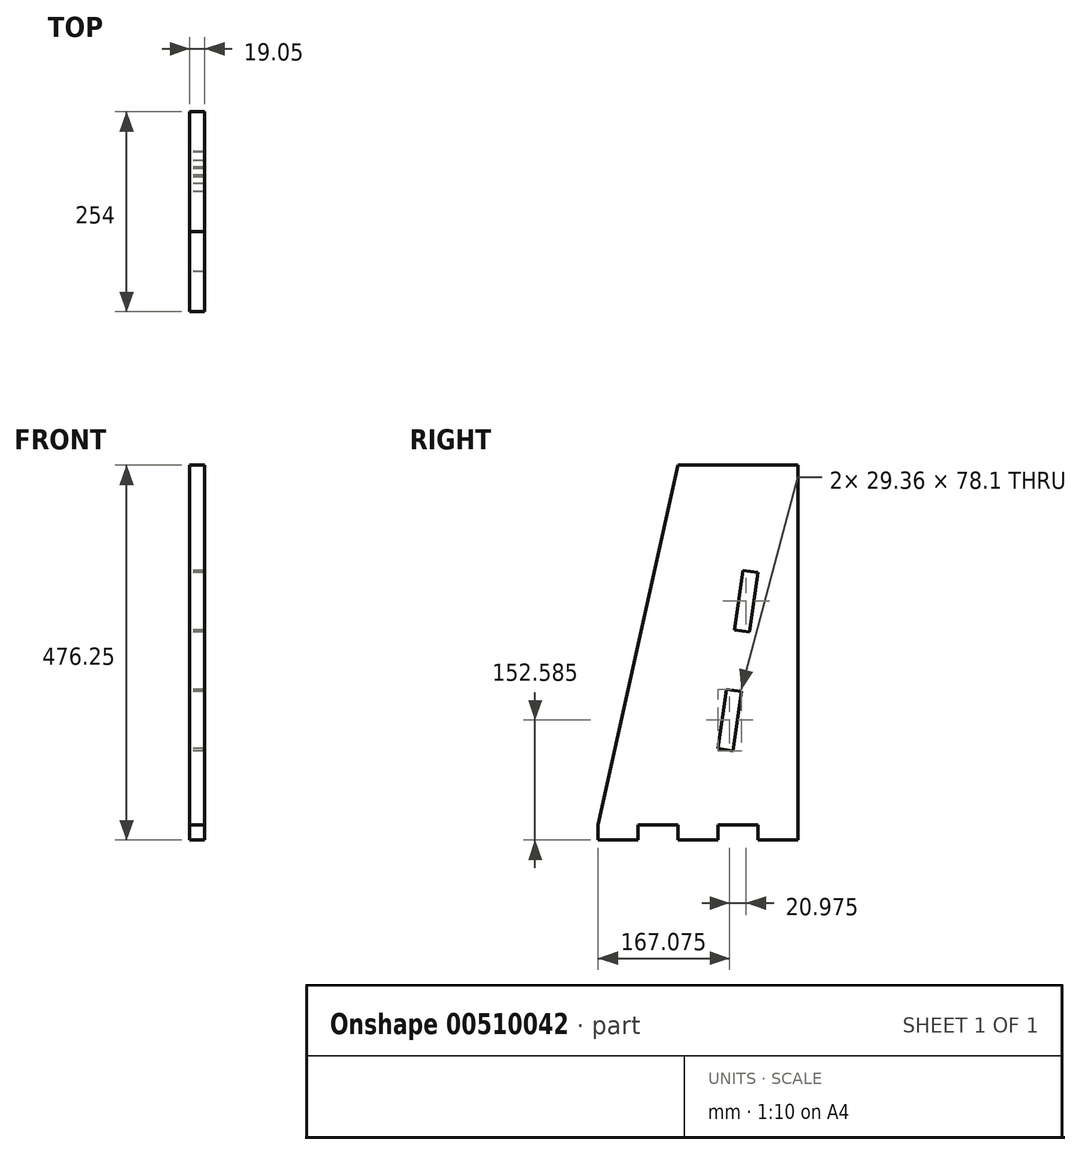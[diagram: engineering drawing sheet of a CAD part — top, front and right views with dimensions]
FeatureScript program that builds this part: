
annotation { "Feature Type Name" : "Feature", "Feature Type Description" : "" }
export const myFeature = defineFeature(function(context is Context, id is Id, definition is map)
    precondition{}
    {
        {
            var Q0;
            Q0=qCreatedBy(makeId("Right.planeOp"),FACE);
            var sketch = newSketch(context, id + "F0", { "sketchPlane" : qUnion([Q0])});
            skLineSegment(sketch, "E0", {"start": v(-38.45, 45.53) * mm, "end": v(113.95, 45.53) * mm});
            skLineSegment(sketch, "E1", {"start": v(113.95, 45.53) * mm, "end": v(113.95, -411.67) * mm});
            skLineSegment(sketch, "E2", {"start": v(-38.45, 45.53) * mm, "end": v(-140.05, -411.67) * mm});
            skLineSegment(sketch, "E3.top", {"start": v(113.95, -430.72) * mm, "end": v(63.15, -430.72) * mm});
            skLineSegment(sketch, "E3.left", {"start": v(113.95, -411.67) * mm, "end": v(113.95, -430.72) * mm});
            skLineSegment(sketch, "E3.right", {"start": v(63.15, -411.67) * mm, "end": v(63.15, -430.72) * mm});
            skLineSegment(sketch, "E4.1.0.0", {"start": v(12.35, -411.67) * mm, "end": v(12.35, -430.72) * mm});
            skLineSegment(sketch, "E4.1.0.1", {"start": v(-38.45, -411.67) * mm, "end": v(-38.45, -430.72) * mm});
            skLineSegment(sketch, "E4.1.0.2", {"start": v(12.35, -430.72) * mm, "end": v(-38.45, -430.72) * mm});
            skLineSegment(sketch, "E4.2.0.0", {"start": v(-89.25, -411.67) * mm, "end": v(-89.25, -430.72) * mm});
            skLineSegment(sketch, "E4.2.0.1", {"start": v(-140.05, -411.67) * mm, "end": v(-140.05, -430.72) * mm});
            skLineSegment(sketch, "E4.2.0.2", {"start": v(-89.25, -430.72) * mm, "end": v(-140.05, -430.72) * mm});
            skLineSegment(sketch, "E4.direction1", {"start": v(63.15, -430.72) * mm, "end": v(-38.45, -430.72) * mm, "construction": true});
            skLineSegment(sketch, "E5", {"start": v(-89.25, -411.67) * mm, "end": v(-38.45, -411.67) * mm});
            skLineSegment(sketch, "E6", {"start": v(12.35, -411.67) * mm, "end": v(63.15, -411.67) * mm});
            skLineSegment(sketch, "E7.bottom", {"start": v(113.95, 45.53) * mm, "end": v(133, 45.53) * mm});
            skLineSegment(sketch, "E7.left", {"start": v(113.95, 45.53) * mm, "end": v(113.95, -30.67) * mm});
            skLineSegment(sketch, "E8.right", {"start": v(113.95, -30.67) * mm, "end": v(113.95, -106.87) * mm});
            skLineSegment(sketch, "E9.bottom", {"start": v(62.68, -90.76) * mm, "end": v(43.8, -88.14) * mm});
            skLineSegment(sketch, "E9.top", {"start": v(52.2, -166.23) * mm, "end": v(33.32, -163.61) * mm});
            skLineSegment(sketch, "E9.right", {"start": v(43.8, -88.14) * mm, "end": v(33.32, -163.61) * mm});
            skLineSegment(sketch, "E10.top", {"start": v(41.7, -241.7) * mm, "end": v(22.83, -239.09) * mm});
            skLineSegment(sketch, "E10.right", {"start": v(113.95, -183.07) * mm, "end": v(113.95, -259.27) * mm});
            skLineSegment(sketch, "E11.top", {"start": v(31.22, -317.18) * mm, "end": v(12.35, -314.56) * mm});
            skLineSegment(sketch, "E11.right", {"start": v(22.83, -239.09) * mm, "end": v(12.35, -314.56) * mm});
            skLineSegment(sketch, "E12.right", {"start": v(113.95, -335.47) * mm, "end": v(113.95, -411.67) * mm});
            skLineSegment(sketch, "E13.left", {"start": v(41.7, -241.7) * mm, "end": v(31.22, -317.18) * mm});
            skLineSegment(sketch, "E14.left", {"start": v(62.68, -90.76) * mm, "end": v(52.2, -166.23) * mm});
            skSolve(sketch);
        }
        {
            var Q0;
            Q0=makeQuery(id+"F0.imprint","IMPRINT",FACE,{"disambiguationData":[TD([[makeQuery(id+"F0.imprint","IMPRINT",EDGE,{"derivedFrom":sQuery(id+"F0.wireOp",EDGE,"E0")}),-1.0]])]});
            extrude(context, id + "F1", {"entities" : qUnion([Q0]), "depth" : 19.05 * mm, "offsetDistance" : 25.4 * mm});
        }
        {
            var Q0;
            Q0 = qSketchRegion(id + "F0", true);
            extrude(context, id + "F2", {"entities" : qUnion([Q0]), "operationType" : NewBodyOperationType.ADD, "depth" : 19.05 * mm, "offsetDistance" : 25.4 * mm});
        }
    });
